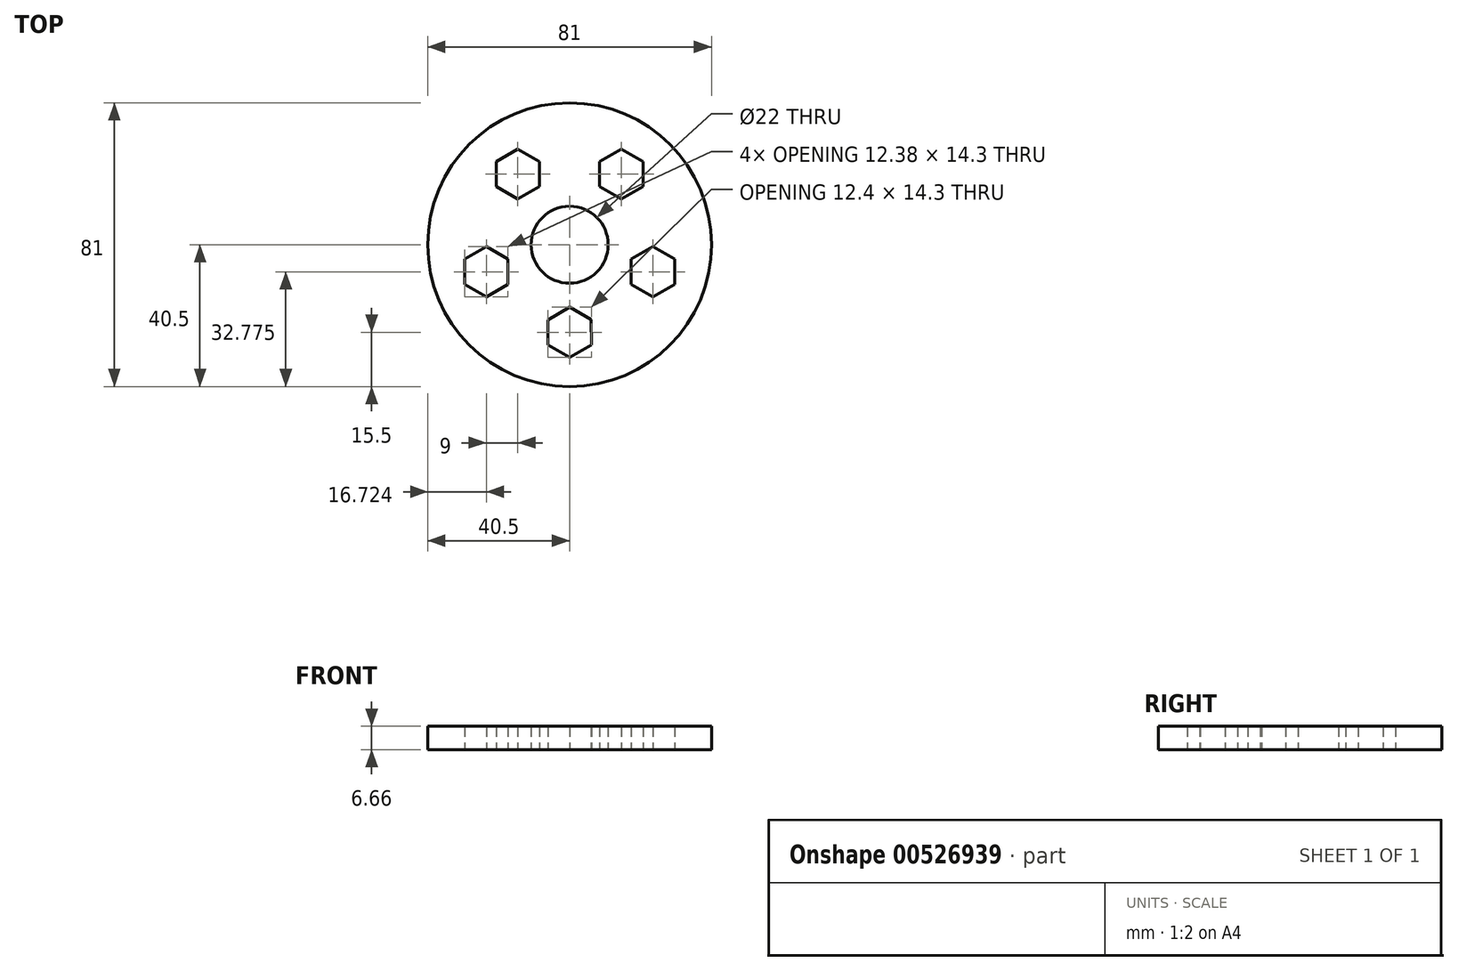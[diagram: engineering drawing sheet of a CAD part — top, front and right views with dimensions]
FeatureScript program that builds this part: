
annotation { "Feature Type Name" : "Feature", "Feature Type Description" : "" }
export const myFeature = defineFeature(function(context is Context, id is Id, definition is map)
    precondition{}
    {
        {
            var Q0;
            Q0=qCreatedBy(makeId("Top.planeOp"),FACE);
            var sketch = newSketch(context, id + "F0", { "sketchPlane" : qUnion([Q0])});
            skPoint(sketch, "E0.0.midPoint", {"position": v(11.9, -3.98) * mm});
            skCircle(sketch, "E1", {"center": v(0, 0) * mm, "radius": 11 * mm});
            skLineSegment(sketch, "E2", {"start": v(0, -25) * mm, "end": v(0, 0) * mm});
            skPoint(sketch, "E3.0.midPoint", {"position": v(-7.58, 20.17) * mm});
            skLineSegment(sketch, "E4.0", {"start": v(20.97, 23.74) * mm, "end": v(20.97, 16.6) * mm});
            skLineSegment(sketch, "E4.1", {"start": v(20.97, 16.6) * mm, "end": v(14.78, 13.02) * mm});
            skLineSegment(sketch, "E4.2", {"start": v(14.78, 13.02) * mm, "end": v(8.58, 16.6) * mm});
            skLineSegment(sketch, "E4.3", {"start": v(8.58, 16.6) * mm, "end": v(8.58, 23.74) * mm});
            skLineSegment(sketch, "E4.4", {"start": v(8.58, 23.74) * mm, "end": v(14.78, 27.32) * mm});
            skLineSegment(sketch, "E4.5", {"start": v(14.78, 27.32) * mm, "end": v(20.97, 23.74) * mm});
            skPoint(sketch, "E4.0.midPoint", {"position": v(20.97, 20.17) * mm});
            skLineSegment(sketch, "E5.0", {"start": v(29.97, -4.15) * mm, "end": v(29.97, -11.3) * mm});
            skLineSegment(sketch, "E5.1", {"start": v(29.97, -11.3) * mm, "end": v(23.78, -14.88) * mm});
            skLineSegment(sketch, "E5.2", {"start": v(23.78, -14.88) * mm, "end": v(17.58, -11.3) * mm});
            skLineSegment(sketch, "E5.3", {"start": v(17.58, -11.3) * mm, "end": v(17.58, -4.15) * mm});
            skLineSegment(sketch, "E5.4", {"start": v(17.58, -4.15) * mm, "end": v(23.78, -0.58) * mm});
            skLineSegment(sketch, "E5.5", {"start": v(23.78, -0.58) * mm, "end": v(29.97, -4.15) * mm});
            skPoint(sketch, "E5.0.midPoint", {"position": v(29.97, -7.73) * mm});
            skLineSegment(sketch, "E6.0", {"start": v(-29.97, -11.3) * mm, "end": v(-29.97, -4.15) * mm});
            skLineSegment(sketch, "E6.1", {"start": v(-29.97, -4.15) * mm, "end": v(-23.78, -0.58) * mm});
            skLineSegment(sketch, "E6.2", {"start": v(-23.78, -0.58) * mm, "end": v(-17.58, -4.15) * mm});
            skLineSegment(sketch, "E6.3", {"start": v(-17.58, -4.15) * mm, "end": v(-17.58, -11.3) * mm});
            skLineSegment(sketch, "E6.4", {"start": v(-17.58, -11.3) * mm, "end": v(-23.78, -14.88) * mm});
            skLineSegment(sketch, "E6.5", {"start": v(-23.78, -14.88) * mm, "end": v(-29.97, -11.3) * mm});
            skPoint(sketch, "E6.0.midPoint", {"position": v(-29.97, -7.73) * mm});
            skPoint(sketch, "E7.0.midPoint", {"position": v(-22.27, 20.17) * mm});
            skPoint(sketch, "E7.0.midPoint.positionSnap0", {"position": v(-19.96, 20.17) * mm});
            skPoint(sketch, "E8.0.midPoint", {"position": v(-31.27, -7.73) * mm});
            skPoint(sketch, "E9.0.midPoint", {"position": v(31.27, -7.73) * mm});
            skPoint(sketch, "E10.0.midPoint", {"position": v(22.27, 20.17) * mm});
            skLineSegment(sketch, "E11.0", {"start": v(6.18, -21.4) * mm, "end": v(6.2, -28.56) * mm});
            skLineSegment(sketch, "E11.1", {"start": v(6.2, -28.56) * mm, "end": v(0.02, -32.15) * mm});
            skLineSegment(sketch, "E11.2", {"start": v(0.02, -32.15) * mm, "end": v(-6.18, -28.6) * mm});
            skLineSegment(sketch, "E11.3", {"start": v(-6.18, -28.6) * mm, "end": v(-6.2, -21.44) * mm});
            skLineSegment(sketch, "E11.4", {"start": v(-6.2, -21.44) * mm, "end": v(-0.02, -17.85) * mm});
            skLineSegment(sketch, "E11.5", {"start": v(-0.02, -17.85) * mm, "end": v(6.18, -21.4) * mm});
            skPoint(sketch, "E11.0.midPoint", {"position": v(6.2, -24.98) * mm});
            skLineSegment(sketch, "E12.0", {"start": v(-8.58, 23.74) * mm, "end": v(-8.58, 16.6) * mm});
            skLineSegment(sketch, "E12.1", {"start": v(-8.58, 16.6) * mm, "end": v(-14.78, 13.02) * mm});
            skLineSegment(sketch, "E12.2", {"start": v(-14.78, 13.02) * mm, "end": v(-20.97, 16.6) * mm});
            skLineSegment(sketch, "E12.3", {"start": v(-20.97, 16.6) * mm, "end": v(-20.97, 23.74) * mm});
            skLineSegment(sketch, "E12.4", {"start": v(-20.97, 23.74) * mm, "end": v(-14.78, 27.32) * mm});
            skLineSegment(sketch, "E12.5", {"start": v(-14.78, 27.32) * mm, "end": v(-8.58, 23.74) * mm});
            skPoint(sketch, "E12.0.midPoint", {"position": v(-8.58, 20.17) * mm});
            skCircle(sketch, "E13", {"center": v(0, 0) * mm, "radius": 40.5 * mm});
            skSolve(sketch);
        }
        {
            var Q0;
            Q0=makeQuery(id+"F0.imprint","IMPRINT",FACE,{"disambiguationData":[TD([[makeQuery(id+"F0.imprint","IMPRINT",EDGE,{"derivedFrom":sQuery(id+"F0.wireOp",EDGE,"E7.0")}),-1.0]])]});
            var Q1;
            Q1=makeQuery(id+"F0.imprint","IMPRINT",FACE,{"disambiguationData":[TD([[makeQuery(id+"F0.imprint","IMPRINT",EDGE,{"derivedFrom":sQuery(id+"F0.wireOp",EDGE,"E4.0")}),1.0]])]});
            var Q2;
            Q2=makeQuery(id+"F0.imprint","IMPRINT",FACE,{"disambiguationData":[TD([[makeQuery(id+"F0.imprint","IMPRINT",EDGE,{"derivedFrom":sQuery(id+"F0.wireOp",EDGE,"E5.0")}),1.0]])]});
            var Q3;
            Q3=makeQuery(id+"F0.imprint","IMPRINT",FACE,{"disambiguationData":[TD([[makeQuery(id+"F0.imprint","IMPRINT",EDGE,{"derivedFrom":sQuery(id+"F0.wireOp",EDGE,"696ce1cd-f161-4916-b882-2e9f835789cf.0")}),-1.0]])]});
            var Q4;
            Q4=makeQuery(id+"F0.imprint","IMPRINT",FACE,{"disambiguationData":[TD([[makeQuery(id+"F0.imprint","IMPRINT",EDGE,{"derivedFrom":sQuery(id+"F0.wireOp",EDGE,"E6.0")}),1.0]])]});
            var Q5;
            {var subQ5=sQuery(id+"F0.wireOp",EDGE,"E0.1");var subQ7=sQuery(id+"F0.wireOp",EDGE,"E0.2");var subQ8=makeQuery(id+"F0.imprint","INTERSECT",VERTEX,{"derivedFrom":[subQ5,subQ7]});Q5=makeQuery(id+"F0.imprint","IMPRINT",FACE,{"disambiguationData":[TD([[makeQuery(id+"F0.imprint","IMPRINT",EDGE,{"disambiguationData":[TD([[subQ8,1.0]])],"derivedFrom":subQ5}),-1.0]])]});}
            var Q6;
            {var subQ5=sQuery(id+"F0.wireOp",EDGE,"E0.3");var subQ6=sQuery(id+"F0.wireOp",EDGE,"E0.2");var subQ7=makeQuery(id+"F0.imprint","INTERSECT",VERTEX,{"derivedFrom":[subQ6,subQ5]});Q6=makeQuery(id+"F0.imprint","IMPRINT",FACE,{"disambiguationData":[TD([[makeQuery(id+"F0.imprint","IMPRINT",EDGE,{"disambiguationData":[TD([[subQ7,1.0]])],"derivedFrom":subQ6}),-1.0]])]});}
            var Q7;
            {var subQ1=sQuery(id+"F0.wireOp",EDGE,"E0.3");var subQ7=sQuery(id+"F0.wireOp",EDGE,"E0.4");var subQ8=makeQuery(id+"F0.imprint","INTERSECT",VERTEX,{"derivedFrom":[subQ1,subQ7]});Q7=makeQuery(id+"F0.imprint","IMPRINT",FACE,{"disambiguationData":[TD([[makeQuery(id+"F0.imprint","IMPRINT",EDGE,{"disambiguationData":[TD([[subQ8,1.0]])],"derivedFrom":subQ1}),-1.0]])]});}
            var Q8;
            {var subQ1=sQuery(id+"F0.wireOp",EDGE,"E0.0");var subQ7=sQuery(id+"F0.wireOp",EDGE,"E0.4");var subQ8=makeQuery(id+"F0.imprint","INTERSECT",VERTEX,{"derivedFrom":[subQ1,subQ7]});Q8=makeQuery(id+"F0.imprint","IMPRINT",FACE,{"disambiguationData":[TD([[makeQuery(id+"F0.imprint","IMPRINT",EDGE,{"disambiguationData":[TD([[subQ8,-1.0]])],"derivedFrom":subQ1}),-1.0]])]});}
            var Q9;
            {var subQ5=sQuery(id+"F0.wireOp",EDGE,"E0.1");var subQ6=sQuery(id+"F0.wireOp",EDGE,"E0.0");var subQ7=makeQuery(id+"F0.imprint","INTERSECT",VERTEX,{"derivedFrom":[subQ6,subQ5]});Q9=makeQuery(id+"F0.imprint","IMPRINT",FACE,{"disambiguationData":[TD([[makeQuery(id+"F0.imprint","IMPRINT",EDGE,{"disambiguationData":[TD([[subQ7,1.0]])],"derivedFrom":subQ6}),-1.0]])]});}
            extrude(context, id + "F1", {"entities" : qUnion([Q0, Q1, Q2, Q3, Q4, Q5, Q6, Q7, Q8, Q9]), "depth" : 6.66 * mm, "offsetDistance" : 25 * mm});
        }
    });
